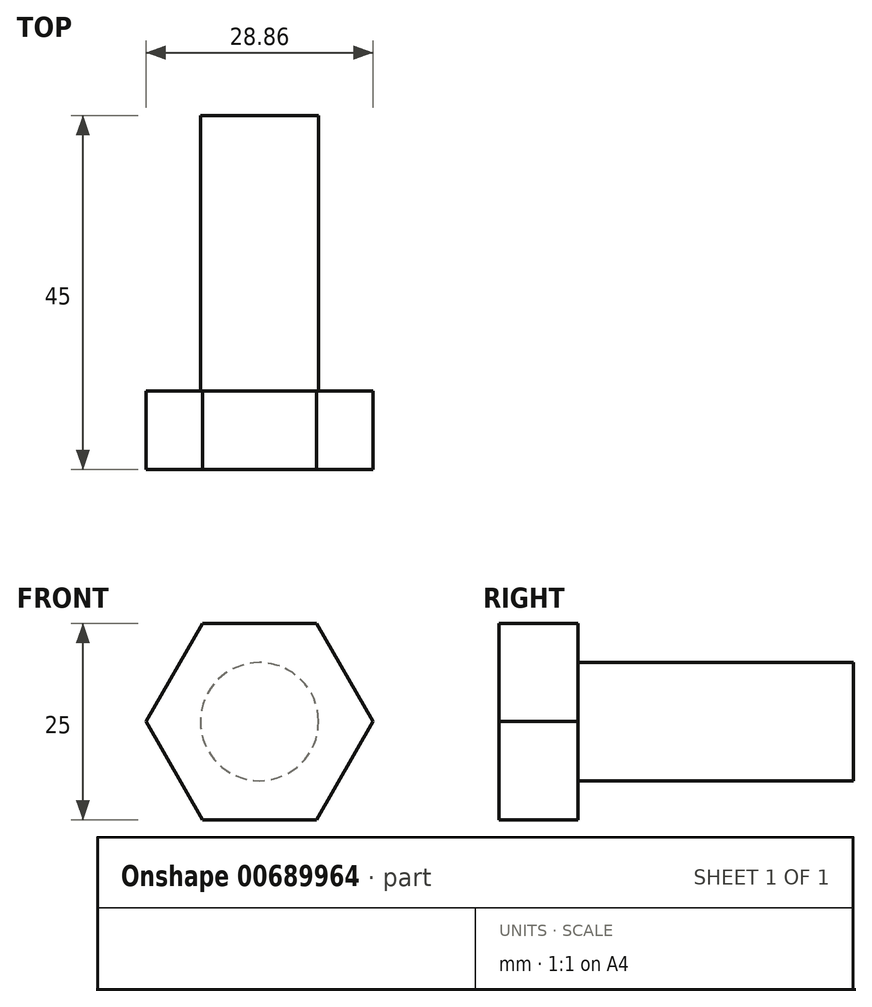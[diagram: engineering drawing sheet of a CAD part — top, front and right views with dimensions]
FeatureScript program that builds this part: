
annotation { "Feature Type Name" : "Feature", "Feature Type Description" : "" }
export const myFeature = defineFeature(function(context is Context, id is Id, definition is map)
    precondition{}
    {
        {
            var Q0;
            Q0=qCreatedBy(makeId("Front.planeOp"),FACE);
            var sketch = newSketch(context, id + "F0", { "sketchPlane" : qUnion([Q0])});
            skCircle(sketch, "E0.cCircle", {"center": v(0, 0) * mm, "radius": 12.5 * mm, "construction": true});
            skLineSegment(sketch, "E0.0", {"start": v(-7.22, 12.5) * mm, "end": v(7.22, 12.5) * mm});
            skLineSegment(sketch, "E0.1", {"start": v(7.22, 12.5) * mm, "end": v(14.43, 0) * mm});
            skLineSegment(sketch, "E0.2", {"start": v(14.43, 0) * mm, "end": v(7.22, -12.5) * mm});
            skLineSegment(sketch, "E0.3", {"start": v(7.22, -12.5) * mm, "end": v(-7.22, -12.5) * mm});
            skLineSegment(sketch, "E0.4", {"start": v(-7.22, -12.5) * mm, "end": v(-14.43, 0) * mm});
            skLineSegment(sketch, "E0.5", {"start": v(-14.43, 0) * mm, "end": v(-7.22, 12.5) * mm});
            skPoint(sketch, "E0.0.midPoint", {"position": v(0, 12.5) * mm});
            skCircle(sketch, "E1", {"center": v(0, 0) * mm, "radius": 7.5 * mm});
            skSolve(sketch);
        }
        {
            var Q0;
            Q0=makeQuery(id+"F0.imprint","IMPRINT",FACE,{"disambiguationData":[TD([[makeQuery(id+"F0.imprint","IMPRINT",EDGE,{"derivedFrom":sQuery(id+"F0.wireOp",EDGE,"E0.0")}),-1.0]])]});
            var Q1;
            Q1=makeQuery(id+"F0.imprint","IMPRINT",FACE,{"disambiguationData":[TD([[makeQuery(id+"F0.imprint","IMPRINT",EDGE,{"derivedFrom":sQuery(id+"F0.wireOp",EDGE,"E1")}),1.0]])]});
            extrude(context, id + "F1", {"entities" : qUnion([Q0, Q1]), "depth" : 10 * mm, "offsetDistance" : 25 * mm});
        }
        {
            var Q0;
            Q0=makeQuery(id+"F0.imprint","IMPRINT",FACE,{"disambiguationData":[TD([[makeQuery(id+"F0.imprint","IMPRINT",EDGE,{"derivedFrom":sQuery(id+"F0.wireOp",EDGE,"E1")}),1.0]])]});
            extrude(context, id + "F2", {"entities" : qUnion([Q0]), "operationType" : NewBodyOperationType.ADD, "oppositeDirection" : true, "depth" : 35 * mm, "offsetDistance" : 25 * mm});
        }
    });
